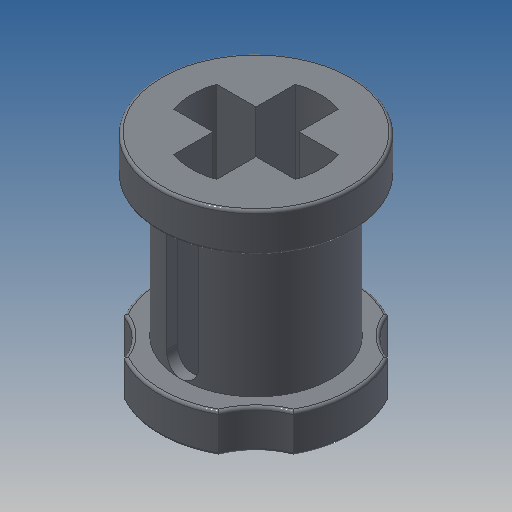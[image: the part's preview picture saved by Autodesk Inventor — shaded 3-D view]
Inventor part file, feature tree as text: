
AUTODESK INVENTOR PART (.ipt)
format: ipt  version: 2022.2 (Build 262287000, 287)  size: 272,896 bytes
history: native  units: mm
features: extrude x5, sketch x4, mirror x1, fillet x1
ambient origin geometry x8: Origin, YZ Plane, XZ Plane, XY Plane, X Axis, Y Axis, Z Axis, Center Point
bodies: Solid2 (feature_tree)
feature tree (11):
  extrude  "Extrusion20"  Depth=5.6mm
  extrude  "Extrusion21"  Depth=4.8mm
  mirror  "Mirror4"
  extrude  "Extrusion23"  Depth=1.6mm
  extrude  "Extrusion24"  Depth=0.1mm TaperAngle=0.0deg
  extrude  "Extrusion29"  Depth=1.44mm TaperAngle=0.0deg
  fillet  "Fillet7"  Radius=1.44mm
  sketch  "Sketch10"  dims[d7=4.76mm d8=0.9mm d9=1.8mm d10=0.9mm d11=1.8mm d65=5.6mm]
  sketch  "Sketch14"  dims[d69=7.2mm d81=4.8mm]
  sketch  "Sketch16"  dims[d82=1.6mm d83=1.6mm]
  sketch  "Sketch22"  dims[d99=1.2mm d110=8.0mm d111=0.0mm d112=1.44mm d113=0.0mm d116=1.44mm d117=0.0mm d118=1.44mm d119=0.0mm d142=8.0mm d143=4.8mm d144=10.0mm d145=0.0mm d146=0.1mm d147=0.0mm d148=0.0mm d149=0.0mm]
